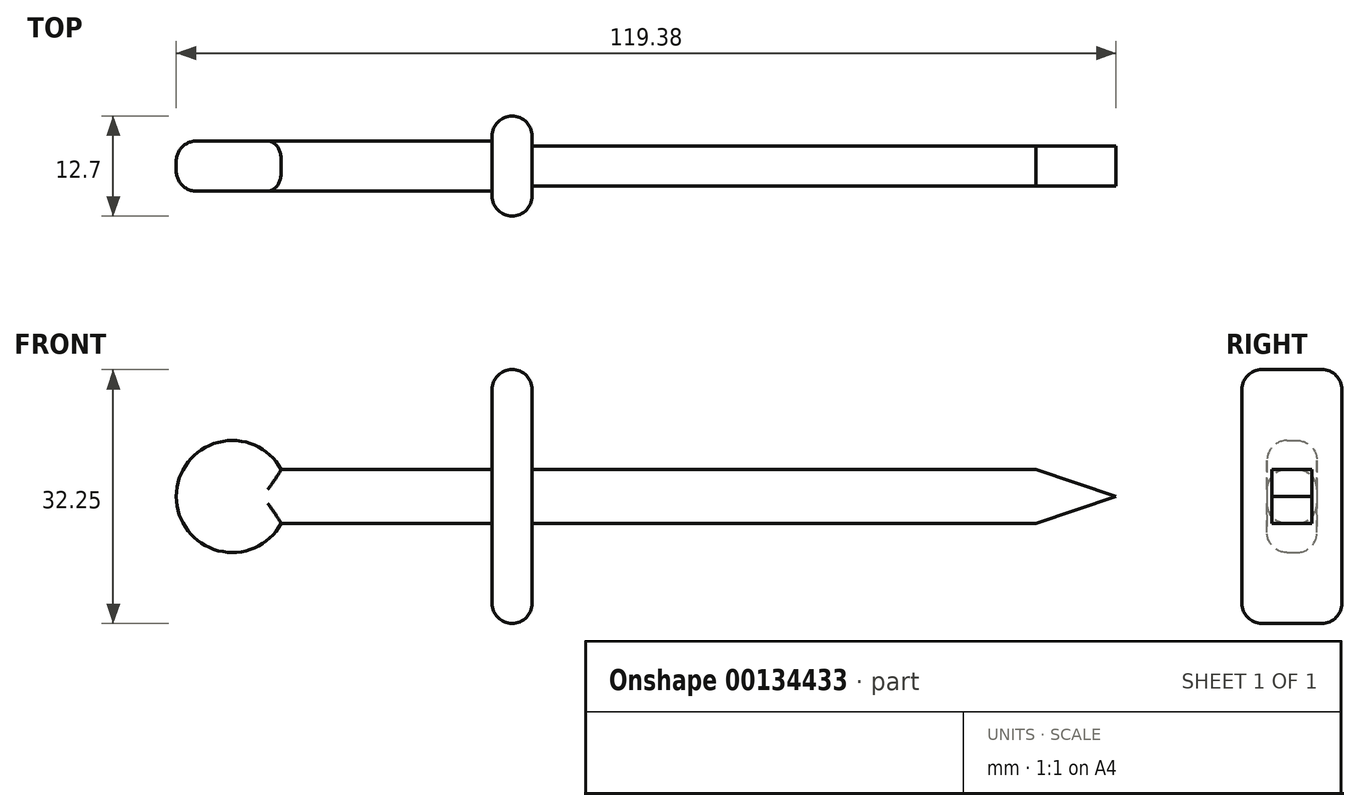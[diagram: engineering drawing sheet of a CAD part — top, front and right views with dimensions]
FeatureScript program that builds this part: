
annotation { "Feature Type Name" : "Feature", "Feature Type Description" : "" }
export const myFeature = defineFeature(function(context is Context, id is Id, definition is map)
    precondition{}
    {
        {
            var Q0;
            Q0=qCreatedBy(makeId("Front.planeOp"),FACE);
            var sketch = newSketch(context, id + "F0", { "sketchPlane" : qUnion([Q0])});
            skLineSegment(sketch, "E0", {"start": v(-36.1, 11.72) * mm, "end": v(-3.08, 11.72) * mm});
            skLineSegment(sketch, "E1", {"start": v(-3.08, 11.72) * mm, "end": v(-3.08, 4.87) * mm});
            skLineSegment(sketch, "E2", {"start": v(-3.08, 4.87) * mm, "end": v(-36.1, 4.87) * mm});
            skLineSegment(sketch, "E3", {"start": v(-36.1, 4.87) * mm, "end": v(-36.1, 11.72) * mm});
            skCircle(sketch, "E4", {"center": v(-36.1, 8.3) * mm, "radius": 7.11 * mm});
            skLineSegment(sketch, "E5", {"start": v(-3.08, 11.72) * mm, "end": v(-3.08, 24.42) * mm});
            skLineSegment(sketch, "E6", {"start": v(-3.08, 4.87) * mm, "end": v(-3.08, -7.83) * mm});
            skLineSegment(sketch, "E7", {"start": v(-3.08, -7.83) * mm, "end": v(2, -7.83) * mm});
            skLineSegment(sketch, "E8", {"start": v(2, -7.83) * mm, "end": v(2, 24.42) * mm});
            skLineSegment(sketch, "E9", {"start": v(2, 24.42) * mm, "end": v(-3.08, 24.42) * mm});
            skLineSegment(sketch, "E10", {"start": v(2, 4.87) * mm, "end": v(66, 4.87) * mm});
            skLineSegment(sketch, "E11", {"start": v(66, 4.87) * mm, "end": v(66, 11.72) * mm});
            skLineSegment(sketch, "E12", {"start": v(66, 11.72) * mm, "end": v(2, 11.72) * mm});
            skLineSegment(sketch, "E13", {"start": v(66, 8.3) * mm, "end": v(76.17, 8.3) * mm});
            skLineSegment(sketch, "E14", {"start": v(66, 4.87) * mm, "end": v(76.17, 8.3) * mm});
            skLineSegment(sketch, "E15", {"start": v(66, 11.72) * mm, "end": v(76.17, 8.3) * mm});
            skSolve(sketch);
        }
        {
            var Q0;
            {var subQ0=sQuery(id+"F0.wireOp",EDGE,"E1");Q0=makeQuery(id+"F0.imprint","IMPRINT",FACE,{"disambiguationData":[TD([[makeQuery(id+"F0.imprint","IMPRINT",EDGE,{"derivedFrom":subQ0}),-1.0]])]});}
            extrude(context, id + "F1", {"entities" : qUnion([Q0]), "endBound" : BoundingType.SYMMETRIC, "depth" : 6.35 * mm});
        }
        {
            var Q0;
            {var subQ0=sQuery(id+"F0.wireOp",EDGE,"E3");Q0=makeQuery(id+"F0.imprint","IMPRINT",FACE,{"disambiguationData":[TD([[makeQuery(id+"F0.imprint","IMPRINT",EDGE,{"derivedFrom":subQ0}),1.0]])]});}
            var Q1;
            {var subQ0=sQuery(id+"F0.wireOp",EDGE,"E3");Q1=makeQuery(id+"F0.imprint","IMPRINT",FACE,{"disambiguationData":[TD([[makeQuery(id+"F0.imprint","IMPRINT",EDGE,{"derivedFrom":subQ0}),-1.0]])]});}
            extrude(context, id + "F2", {"entities" : qUnion([Q0, Q1]), "operationType" : NewBodyOperationType.ADD, "endBound" : BoundingType.SYMMETRIC, "depth" : 6.35 * mm});
        }
        {
            var Q0;
            Q0=makeQuery(id+"F2.opExtrude","CAP_EDGE",EDGE,{"disambiguationData":[OSD([sQuery(id+"F0.wireOp",EDGE,"E4")])],"isStart":false});
            var Q1;
            Q1=makeQuery(id+"F1.opExtrude","CAP_EDGE",EDGE,{"disambiguationData":[OSD([sQuery(id+"F0.wireOp",EDGE,"E0")])],"isStart":false});
            var Q2;
            Q2=makeQuery(id+"F2.opExtrude","CAP_EDGE",EDGE,{"disambiguationData":[OSD([sQuery(id+"F0.wireOp",EDGE,"E4")])],"isStart":true});
            var Q3;
            Q3=makeQuery(id+"F1.opExtrude","CAP_EDGE",EDGE,{"disambiguationData":[OSD([sQuery(id+"F0.wireOp",EDGE,"E0")])],"isStart":true});
            var Q4;
            Q4=makeQuery(id+"F1.opExtrude","CAP_EDGE",EDGE,{"disambiguationData":[OSD([sQuery(id+"F0.wireOp",EDGE,"E2")])],"isStart":false});
            var Q5;
            Q5=makeQuery(id+"F1.opExtrude","CAP_EDGE",EDGE,{"disambiguationData":[OSD([sQuery(id+"F0.wireOp",EDGE,"E2")])],"isStart":true});
            fillet(context, id + "F3", {"entities" : qUnion([Q0, Q1, Q2, Q3, Q4, Q5]), "radius" : 2.54 * mm, "tangentPropagation" : true, "allowEdgeOverflow" : false});
        }
        {
            var Q0;
            Q0=makeQuery(id+"F0.imprint","IMPRINT",FACE,{"disambiguationData":[TD([[makeQuery(id+"F0.imprint","IMPRINT",EDGE,{"derivedFrom":sQuery(id+"F0.wireOp",EDGE,"E1")}),1.0]])]});
            extrude(context, id + "F4", {"entities" : qUnion([Q0]), "operationType" : NewBodyOperationType.ADD, "endBound" : BoundingType.SYMMETRIC, "depth" : 12.7 * mm});
        }
        {
            var Q0;
            Q0=makeQuery(id+"F4.opExtrude","CAP_EDGE",EDGE,{"disambiguationData":[OSD([sQuery(id+"F0.wireOp",EDGE,"E9")])],"isStart":false});
            var Q1;
            Q1=makeQuery(id+"F4.opExtrude","CAP_EDGE",EDGE,{"disambiguationData":[OSD([sQuery(id+"F0.wireOp",EDGE,"E7")])],"isStart":false});
            var Q2;
            Q2=makeQuery(id+"F4.opExtrude","CAP_EDGE",EDGE,{"disambiguationData":[OSD([sQuery(id+"F0.wireOp",EDGE,"E9")])],"isStart":true});
            var Q3;
            Q3=makeQuery(id+"F4.opExtrude","CAP_EDGE",EDGE,{"disambiguationData":[OSD([sQuery(id+"F0.wireOp",EDGE,"E7")])],"isStart":true});
            var Q4;
            Q4=makeQuery(id+"F4.opExtrude","SWEPT_EDGE",EDGE,{"disambiguationData":[OSD([sQuery(id+"F0.wireOp",EDGE,"E7"),sQuery(id+"F0.wireOp",EDGE,"E8")])]});
            var Q5;
            Q5=makeQuery(id+"F4.opExtrude","SWEPT_EDGE",EDGE,{"disambiguationData":[OSD([sQuery(id+"F0.wireOp",EDGE,"E8"),sQuery(id+"F0.wireOp",EDGE,"E9")])]});
            var Q6;
            Q6=makeQuery(id+"F4.opExtrude","CAP_EDGE",EDGE,{"disambiguationData":[OSD([sQuery(id+"F0.wireOp",EDGE,"E8")])],"isStart":true});
            var Q7;
            Q7=makeQuery(id+"F4.opExtrude","CAP_EDGE",EDGE,{"disambiguationData":[OSD([sQuery(id+"F0.wireOp",EDGE,"E8")])],"isStart":false});
            var Q8;
            Q8=makeQuery(id+"F4.opExtrude","SWEPT_EDGE",EDGE,{"disambiguationData":[OSD([sQuery(id+"F0.wireOp",EDGE,"E6"),sQuery(id+"F0.wireOp",EDGE,"E7")])]});
            var Q9;
            Q9=makeQuery(id+"F4.opExtrude","CAP_EDGE",EDGE,{"disambiguationData":[OSD([sQuery(id+"F0.wireOp",EDGE,"E1"),sQuery(id+"F0.wireOp",EDGE,"E5"),sQuery(id+"F0.wireOp",EDGE,"E6")])],"isStart":true});
            var Q10;
            Q10=makeQuery(id+"F4.opExtrude","SWEPT_EDGE",EDGE,{"disambiguationData":[OSD([sQuery(id+"F0.wireOp",EDGE,"E5"),sQuery(id+"F0.wireOp",EDGE,"E9")])]});
            var Q11;
            Q11=makeQuery(id+"F4.opExtrude","CAP_EDGE",EDGE,{"disambiguationData":[OSD([sQuery(id+"F0.wireOp",EDGE,"E1"),sQuery(id+"F0.wireOp",EDGE,"E5"),sQuery(id+"F0.wireOp",EDGE,"E6")])],"isStart":false});
            fillet(context, id + "F5", {"entities" : qUnion([Q0, Q1, Q2, Q3, Q4, Q5, Q6, Q7, Q8, Q9, Q10, Q11]), "radius" : 2.54 * mm, "tangentPropagation" : true, "allowEdgeOverflow" : false});
        }
        {
            var Q0;
            {var subQ3=sQuery(id+"F0.wireOp",EDGE,"E10");Q0=makeQuery(id+"F0.imprint","IMPRINT",FACE,{"disambiguationData":[TD([[makeQuery(id+"F0.imprint","IMPRINT",EDGE,{"derivedFrom":subQ3}),1.0]])]});}
            var Q1;
            {var subQ2=sQuery(id+"F0.wireOp",EDGE,"E13");Q1=makeQuery(id+"F0.imprint","IMPRINT",FACE,{"disambiguationData":[TD([[makeQuery(id+"F0.imprint","IMPRINT",EDGE,{"derivedFrom":subQ2}),1.0]])]});}
            var Q2;
            {var subQ2=sQuery(id+"F0.wireOp",EDGE,"E13");Q2=makeQuery(id+"F0.imprint","IMPRINT",FACE,{"disambiguationData":[TD([[makeQuery(id+"F0.imprint","IMPRINT",EDGE,{"derivedFrom":subQ2}),-1.0]])]});}
            extrude(context, id + "F6", {"entities" : qUnion([Q0, Q1, Q2]), "operationType" : NewBodyOperationType.ADD, "endBound" : BoundingType.SYMMETRIC, "depth" : 5.08 * mm});
        }
    });
